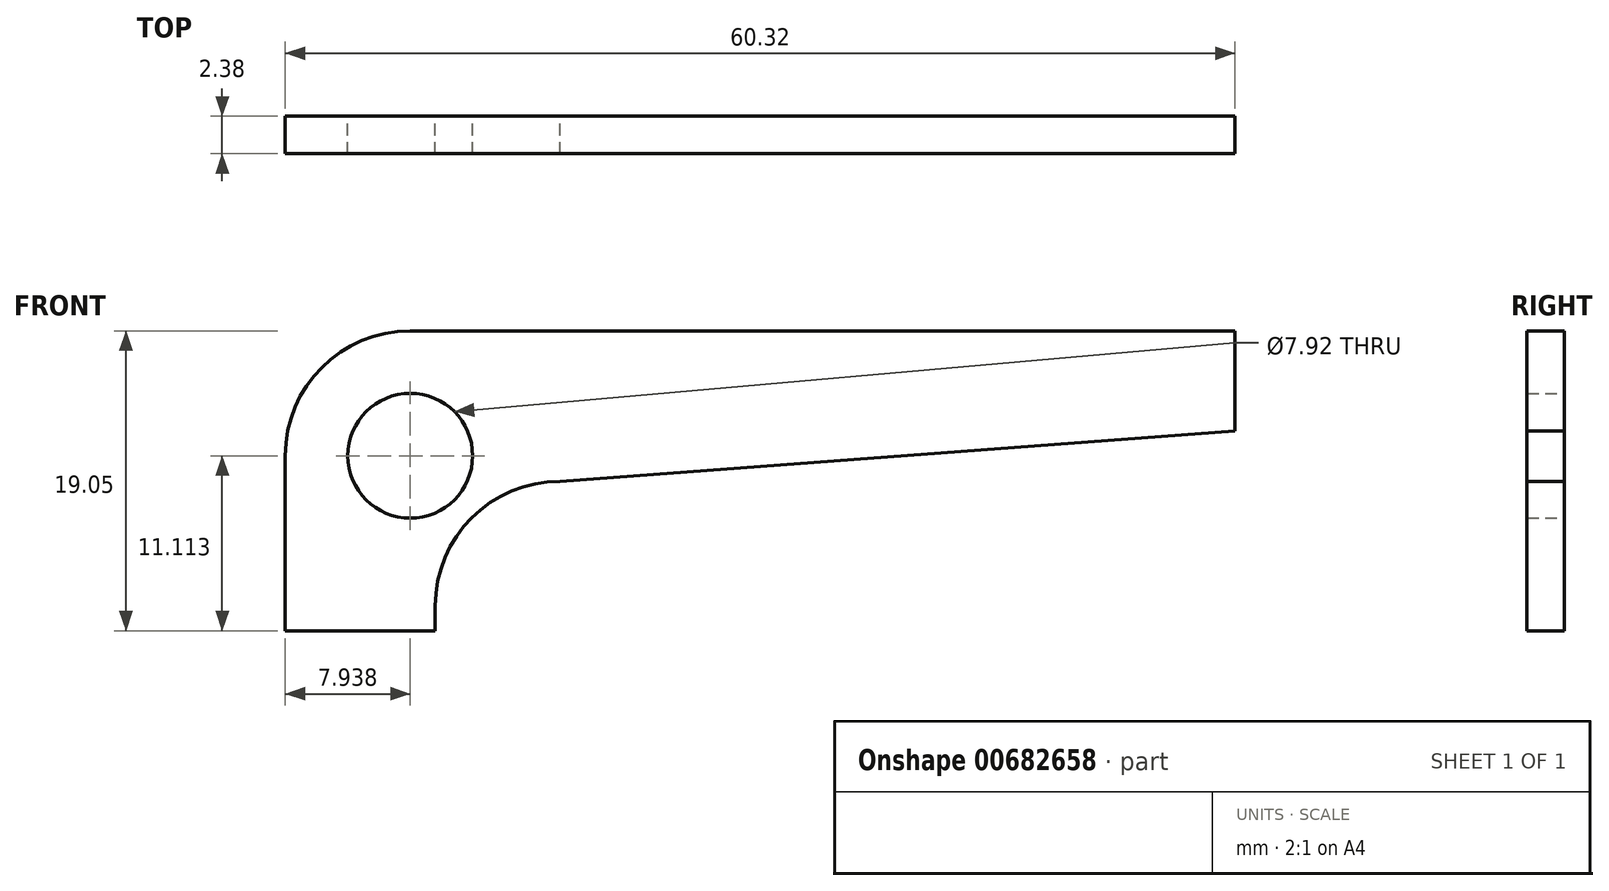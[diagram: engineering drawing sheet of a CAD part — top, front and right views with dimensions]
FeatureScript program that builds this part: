
annotation { "Feature Type Name" : "Feature", "Feature Type Description" : "" }
export const myFeature = defineFeature(function(context is Context, id is Id, definition is map)
    precondition{}
    {
        {
            var Q0;
            Q0=qCreatedBy(makeId("Front.planeOp"),FACE);
            var sketch = newSketch(context, id + "F0", { "sketchPlane" : qUnion([Q0])});
            skLineSegment(sketch, "E0.bottom", {"start": v(0, 0) * mm, "end": v(9.52, 0) * mm});
            skLineSegment(sketch, "E0.top", {"start": v(7.94, 19.05) * mm, "end": v(60.33, 19.05) * mm});
            skLineSegment(sketch, "E0.left", {"start": v(0, 0) * mm, "end": v(0, 11.11) * mm});
            skLineSegment(sketch, "E0.right", {"start": v(60.33, 12.7) * mm, "end": v(60.33, 19.05) * mm});
            skLineSegment(sketch, "E1", {"start": v(60.33, 19.05) * mm, "end": v(60.33, 12.7) * mm});
            skPoint(sketch, "E2.visualSharp", {"position": v(0, 19.05) * mm});
            skArc(sketch, "E2.filletArc", {"start": v(7.94, 19.05) * mm, "mid": v(2.32, 16.73) * mm, "end": v(0, 11.11) * mm});
            skLineSegment(sketch, "E3", {"start": v(0, 11.11) * mm, "end": v(0, 5.56) * mm});
            skLineSegment(sketch, "E4", {"start": v(0, 0) * mm, "end": v(9.53, 0) * mm});
            skLineSegment(sketch, "E5", {"start": v(9.53, 0) * mm, "end": v(9.53, 1.57) * mm});
            skPoint(sketch, "E6.end.orphan", {"position": v(9.52, 12.7) * mm});
            skArc(sketch, "E7.filletArc", {"start": v(17.45, 9.5) * mm, "mid": v(11.85, 7.17) * mm, "end": v(9.53, 1.57) * mm});
            skLineSegment(sketch, "E8", {"start": v(60.33, 12.7) * mm, "end": v(17.45, 9.5) * mm});
            skCircle(sketch, "E9", {"center": v(7.94, 11.11) * mm, "radius": 3.96 * mm});
            skSolve(sketch);
        }
        {
            var Q0;
            Q0 = qSketchRegion(id + "F0", true);
            extrude(context, id + "F1", {"entities" : qUnion([Q0]), "depth" : 2.38 * mm, "offsetDistance" : 25.4 * mm});
        }
    });
